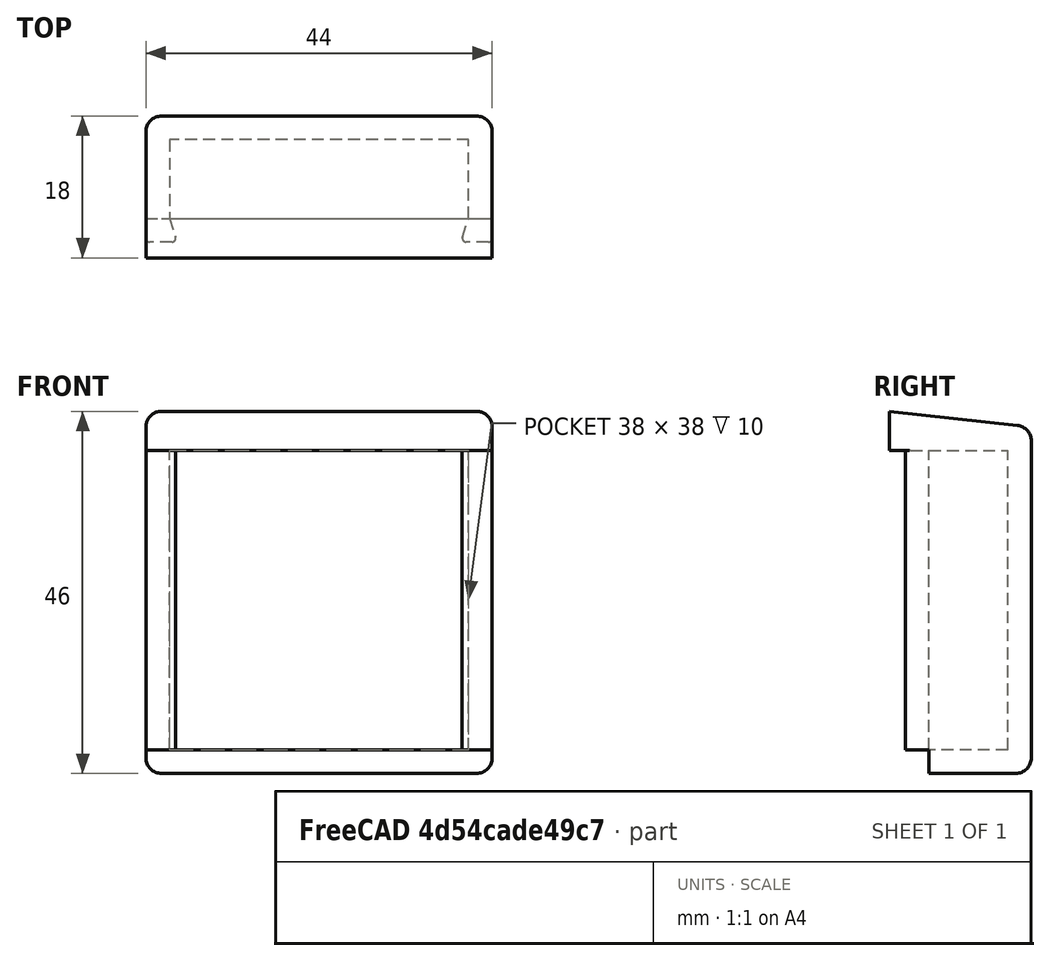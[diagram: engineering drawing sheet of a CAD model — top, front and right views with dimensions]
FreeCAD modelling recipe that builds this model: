
FCSTD DOCUMENT  (FreeCAD 0.21R33668 +26 (Git))
Label: Box_8
License: All rights reserved
LicenseURL: http://en.wikipedia.org/wiki/All_rights_reserved
objects: Sketcher::SketchObject×4, PartDesign::Pad×3, PartDesign::Plane×3, PartDesign::Fillet×2, PartDesign::Pocket×1, PartDesign::Body×1, Mesh::Feature×1
note: 20 computed .brp shape members not serialized (recipe doc carries the construction recipe); baked Part::Feature solids carry a one-line shape summary decoded from their .brp

FEATURE [Sketcher::SketchObject] Sketch
  FullyConstrained = true
  MapMode = 5
  Support = -> [XY_Plane]
  sketch-geometry (10):
    g0: LineSegment StartX=0 StartY=-3 StartZ=0 EndX=0 EndY=13 EndZ=0
    g1: LineSegment StartX=0 StartY=13 StartZ=0 EndX=44 EndY=13 EndZ=0
    g2: LineSegment StartX=44 StartY=13 StartZ=0 EndX=44 EndY=-3 EndZ=0
    g3: LineSegment StartX=44 StartY=-3 StartZ=0 EndX=40 EndY=-3 EndZ=0
    g4: LineSegment StartX=40 StartY=-3 StartZ=0 EndX=41 EndY=0 EndZ=0
    g5: LineSegment StartX=41 StartY=0 StartZ=0 EndX=41 EndY=10 EndZ=0
    g6: LineSegment StartX=41 StartY=10 StartZ=0 EndX=3 EndY=10 EndZ=0
    g7: LineSegment StartX=3 StartY=10 StartZ=0 EndX=3 EndY=0 EndZ=0
    g8: LineSegment StartX=3 StartY=0 StartZ=0 EndX=4 EndY=-3 EndZ=0
    g9: LineSegment StartX=4 StartY=-3 StartZ=0 EndX=0 EndY=-3 EndZ=0
  constraints (30):
    c: PointOnObject(g0,g-2)
    c: PointOnObject(g0,g-2)
    c: Coincident(g0,g1)
    c: Horizontal(g1)
    c: Coincident(g1,g2)
    c: Vertical(g2)
    c: Coincident(g2,g3)
    c: Horizontal(g3)
    c: Coincident(g3,g4)
    c: PointOnObject(g4,g-1)
    c: Coincident(g4,g5)
    c: Vertical(g5)
    c: Coincident(g5,g6)
    c: Horizontal(g6)
    c: Coincident(g6,g7)
    c: PointOnObject(g7,g-1)
    c: Vertical(g7)
    c: Coincident(g7,g8)
    c: Coincident(g8,g9)
    c: Coincident(g9,g0)
    c: Horizontal(g9)
    c: Equal(g9,g3)
    c: DistanceX(g3,g3) = 4
    c: DistanceX(g5,g1) = 3
    c: DistanceX(g0,g6) = 3
    c: DistanceY(g6,g0) = 3
    c: DistanceY(g0) = -3
    c: Horizontal(g0,g2)
    c: DistanceX(g6,g6) = 38
    c: DistanceY(g6) = 10
FEATURE [PartDesign::Pad] Pad
  Direction = (0,0,1)
  Length = 38
  Length2 = 10
  Profile = -> Sketch
  ReferenceAxis = -> Sketch [N_Axis]
  Refine = true
  Type = 0
FEATURE [PartDesign::Plane] DatumPlane
  Length = 60
  MapMode = 5
  Placement = pos=(0,0,38) rot=(0,0,1;0rad)
  ResizeMode = 0
  Support = -> [Pad]
  Width = 60
FEATURE [Sketcher::SketchObject] Sketch001
  ExternalGeometry = -> [Pad]
  FullyConstrained = true
  MapMode = 5
  Placement = pos=(0,0,38) rot=(0,0,1;0rad)
  Support = -> [DatumPlane]
  sketch-geometry (4):
    g0: LineSegment StartX=0 StartY=13 StartZ=0 EndX=44 EndY=13 EndZ=0
    g1: LineSegment StartX=44 StartY=13 StartZ=0 EndX=44 EndY=-5 EndZ=0
    g2: LineSegment StartX=44 StartY=-5 StartZ=0 EndX=0 EndY=-5 EndZ=0
    g3: LineSegment StartX=0 StartY=-5 StartZ=0 EndX=0 EndY=13 EndZ=0
  constraints (11):
    c: Coincident(g0,g1)
    c: Coincident(g1,g2)
    c: Coincident(g2,g3)
    c: Coincident(g3,g0)
    c: Horizontal(g0)
    c: Horizontal(g2)
    c: Vertical(g1)
    c: Vertical(g3)
    c: Coincident(g0,g-3)
    c: DistanceX(g0,g0) = 44
    c: DistanceY(g2) = -5
FEATURE [PartDesign::Pad] Pad001
  BaseFeature = -> Pad
  Direction = (0,0,1)
  Length = 5
  Length2 = 10
  Profile = -> Sketch001
  ReferenceAxis = -> Sketch001 [N_Axis]
  Refine = true
  Type = 0
FEATURE [PartDesign::Plane] DatumPlane001
  Length = 60
  MapMode = 5
  Placement = pos=(0,0,0) rot=(1,0,0;3.14159rad)
  ResizeMode = 0
  Support = -> [Pad001]
  Width = 60
FEATURE [Sketcher::SketchObject] Sketch002
  ExternalGeometry = -> [Pad001]
  FullyConstrained = true
  MapMode = 5
  Placement = pos=(0,0,0) rot=(1,0,0;3.14159rad)
  Support = -> [DatumPlane001]
  sketch-geometry (4):
    g0: LineSegment StartX=0 StartY=0 StartZ=0 EndX=44 EndY=0 EndZ=0
    g1: LineSegment StartX=44 StartY=0 StartZ=0 EndX=44 EndY=-13 EndZ=0
    g2: LineSegment StartX=44 StartY=-13 StartZ=0 EndX=0 EndY=-13 EndZ=0
    g3: LineSegment StartX=0 StartY=-13 StartZ=0 EndX=0 EndY=0 EndZ=0
  constraints (10):
    c: Coincident(g0,g1)
    c: Coincident(g1,g2)
    c: Coincident(g2,g3)
    c: Coincident(g3,g0)
    c: Horizontal(g0)
    c: Horizontal(g2)
    c: Vertical(g1)
    c: Vertical(g3)
    c: Coincident(g0,g-1)
    c: Coincident(g1,g-3)
FEATURE [PartDesign::Pad] Pad002
  BaseFeature = -> Pad001
  Direction = (0,0,-1)
  Length = 3
  Length2 = 10
  Profile = -> Sketch002
  ReferenceAxis = -> Sketch002 [N_Axis]
  Refine = true
  Type = 0
FEATURE [PartDesign::Plane] DatumPlane002
  Length = 60
  MapMode = 5
  Placement = pos=(44,0,0) rot=(0.57735,0.57735,0.57735;2.0944rad)
  ResizeMode = 0
  Support = -> [Pad002]
  Width = 60
FEATURE [Sketcher::SketchObject] Sketch003
  ExternalGeometry = -> [Pad002]
  FullyConstrained = true
  MapMode = 5
  Placement = pos=(44,0,0) rot=(0.57735,0.57735,0.57735;2.0944rad)
  Support = -> [DatumPlane002]
  sketch-geometry (3):
    g0: LineSegment StartX=-5 StartY=43 StartZ=0 EndX=13 EndY=43 EndZ=0
    g1: LineSegment StartX=13 StartY=43 StartZ=0 EndX=13 EndY=41 EndZ=0
    g2: LineSegment StartX=13 StartY=41 StartZ=0 EndX=-5 EndY=43 EndZ=0
  constraints (7):
    c: Coincident(g-5,g0)
    c: Coincident(g0,g-4)
    c: Coincident(g0,g1)
    c: PointOnObject(g1,g-4)
    c: Coincident(g1,g2)
    c: Coincident(g2,g0)
    c: DistanceY(g1,g1) = 2
FEATURE [PartDesign::Pocket] Pocket
  BaseFeature = -> Pad002
  Direction = (-1,0,0)
  Length = 5
  Length2 = 5
  Profile = -> Sketch003
  ReferenceAxis = -> Sketch003 [N_Axis]
  Refine = true
  Type = 2
FEATURE [PartDesign::Fillet] Fillet
  Base = -> Pocket [Edge33,Edge12,Edge32,Edge31,Edge11,Edge29,Edge10,Edge30]
  BaseFeature = -> Pocket
  Radius = 2
  Refine = true
  SupportTransform = false
  UseAllEdges = false
FEATURE [PartDesign::Fillet] Fillet001
  Base = -> Fillet [Edge5,Edge23,Edge65,Edge50]
  BaseFeature = -> Fillet
  Radius = 0.5
  Refine = true
  SupportTransform = false
  UseAllEdges = false
FEATURE [PartDesign::Body] Body
  Group = -> [Sketch,Pad,DatumPlane,Sketch001,Pad001,DatumPlane001,Sketch002,Pad002,DatumPlane002,Sketch003,Pocket,Fillet,Fillet001]
  Origin = -> Origin
  Tip = -> Fillet001
FEATURE [Mesh::Feature] Mesh  label="Fillet001 (Meshed)"
